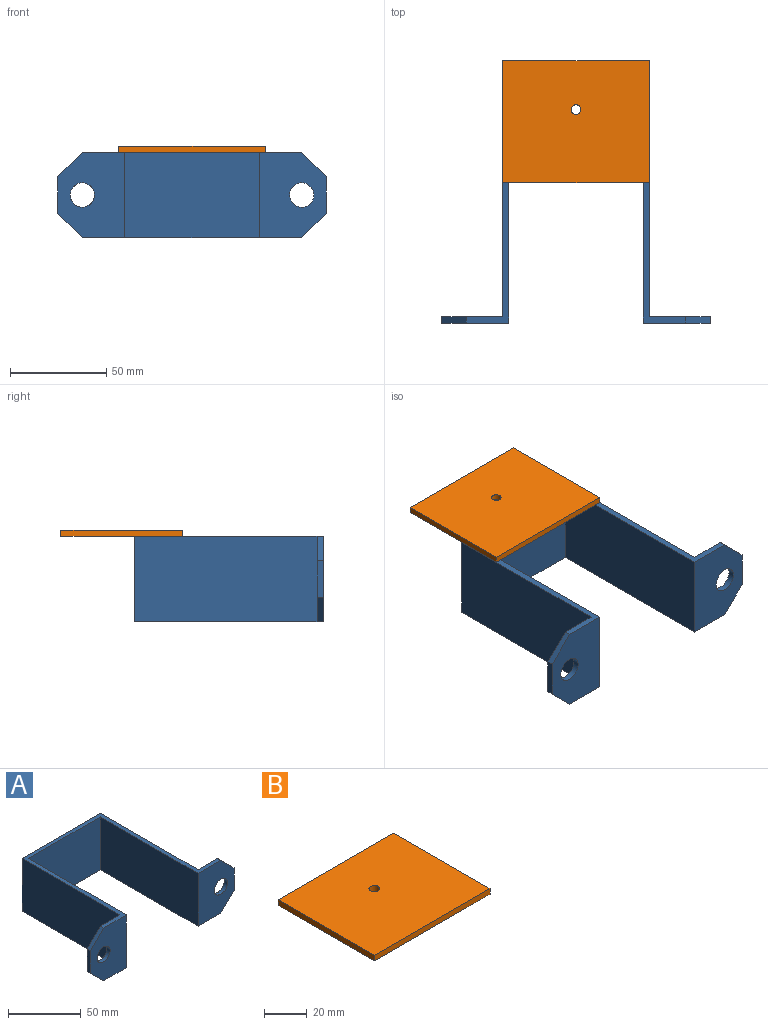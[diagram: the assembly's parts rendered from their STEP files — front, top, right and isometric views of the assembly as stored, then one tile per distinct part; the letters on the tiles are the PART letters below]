
ASSEMBLY  parts=2 mates=1
PART A: 20 faces, bbox 139.7x98.4x44.5 mm
  f0: plane 95.25x44.45mm, normal (1,0,0), area 4233.9mm2, adj f1,f11,f12,f13
  f1: plane 69.85x44.45mm, normal (0,-1,0), area 3104.8mm2, adj f0,f2,f12,f13
  f2: plane 95.25x44.45mm, normal (-1,0,0), area 4233.9mm2, adj f1,f3,f12,f13
  f3: plane 44.45x34.93mm, normal (0,-1,0), area 1264.4mm2, adj f2,f4,f12,f13,f15,f18,f19
  f4: plane 19.05x3.18mm, normal (1,0,0), area 60.5mm2, adj f3,f5,f18,f19
  f5: plane 44.45x31.75mm, normal (0,1,0), area 1123.3mm2, adj f4,f6,f12,f13,f15,f18,f19
  f6: plane 95.25x44.45mm, normal (1,0,0), area 4233.9mm2, adj f5,f7,f12,f13
  f7: plane 76.2x44.45mm, normal (0,1,0), area 3387.1mm2, adj f6,f8,f12,f13
  f8: plane 95.25x44.45mm, normal (-1,0,0), area 4233.9mm2, adj f7,f9,f12,f13
  f9: plane 44.45x31.75mm, normal (0,1,0), area 1123.3mm2, adj f8,f10,f12,f13,f14,f16,f17
  f10: plane 19.05x3.18mm, normal (-1,0,0), area 60.5mm2, adj f9,f11,f16,f17
  f11: plane 44.45x34.93mm, normal (0,-1,0), area 1264.4mm2, adj f0,f10,f12,f13,f14,f16,f17
  f12: plane 114.3x98.43mm, normal (0,0,1), area 967.7mm2, adj f0,f1,f2,f3,f5,f6,f7,f8
  f13: plane 114.3x98.43mm, normal (0,0,-1), area 967.7mm2, adj f0,f1,f2,f3,f5,f6,f7,f8
  f14: cylinder r=6.35mm len=12.7mm, axis (0,1,0), area 126.7mm2, adj f9,f11
  f15: cylinder r=6.35mm len=12.7mm, axis (0,1,0), area 126.7mm2, adj f3,f5
  f16: plane 12.7x12.7mm, normal (-0.71,0,-0.71), area 57mm2, adj f9,f10,f11,f13
  f17: plane 12.7x12.7mm, normal (-0.71,0,0.71), area 57mm2, adj f9,f10,f11,f12
  f18: plane 12.7x12.7mm, normal (0.71,0,-0.71), area 57mm2, adj f3,f4,f5,f13
  f19: plane 12.7x12.7mm, normal (0.71,0,0.71), area 57mm2, adj f3,f4,f5,f12
PART B: 7 faces, bbox 76.2x63.5x3.2 mm
  f0: plane 63.5x3.18mm, normal (1,0,0), area 201.6mm2, adj f1,f3,f5,f6
  f1: plane 76.2x3.18mm, normal (0,1,0), area 241.9mm2, adj f0,f2,f5,f6
  f2: plane 63.5x3.18mm, normal (-1,0,0), area 201.6mm2, adj f1,f3,f5,f6
  f3: plane 76.2x3.18mm, normal (0,-1,0), area 241.9mm2, adj f0,f2,f5,f6
  f4: cylinder r=2.5mm len=5mm, axis (0,0,-1), area 49.9mm2, adj f5,f6
  f5: plane 76.2x63.5mm, normal (0,0,1), area 4819.1mm2, adj f0,f1,f2,f3,f4
  f6: plane 76.2x63.5mm, normal (0,0,-1), area 4819.1mm2, adj f0,f1,f2,f3,f4
PLACE A t=(-10.8,13.58,-13.02)mm
PLACE B t=(-10.8,23.11,31.43)mm
MATE fastened A.f12 <-> B.f6  axis (0,0,-1) through (27.3,16.76,31.43)mm
